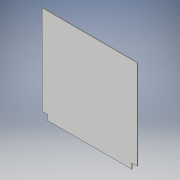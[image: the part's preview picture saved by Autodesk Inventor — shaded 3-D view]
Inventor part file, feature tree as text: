
AUTODESK INVENTOR PART (.ipt)
format: ipt  version: 2018 (Build 220112000, 112)  size: 102,400 bytes
history: native  units: in
note: dims shown in document units (in); Inventor stores cm internally (conversion verified against a paired STEP export)
features: extrude x2, sketch x2
ambient origin geometry x8: Origin, YZ Plane, XZ Plane, XY Plane, X Axis, Y Axis, Z Axis, Center Point
bodies: Solid1 (feature_tree)
feature tree (4):
  extrude  "Extrusion1"  Depth=18.0in
  extrude  "Extrusion2"  Depth=1.0in
  sketch  "Sketch1"  dims[d0=18.0in d1=18.0in]
  sketch  "Sketch2"  dims[d2=0.1in d3=0.0in d4=1.0in d5=1.0in d6=1.0in d7=1.0in d8=1.0in d9=0.0in]
